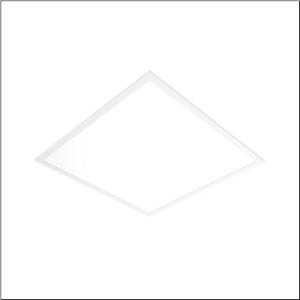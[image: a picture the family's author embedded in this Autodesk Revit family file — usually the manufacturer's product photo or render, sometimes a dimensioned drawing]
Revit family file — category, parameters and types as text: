
# Revit family: apollon_r__41_51mh11wm2443_3aa7
name_source: partatom
category: Lighting Fixtures
units: mm (PartAtom-declared; Revit-internal decimal feet)

## family parameters
Cut with Voids When Loaded = No
Host = Face
Light Source = No
Part Type = Normal
Room Calculation Point = No
Round Connector Dimension = Use Diameter
Shared = No

## types (1)
- --- (1 x LED, 4380 lm, 35 W, 4000K)
    Apparent Load = 35 VA
    CIE Flux Codes = 61 87 97 100 100
    Color Rendering = 80
    Color Temperature = 4000K
    Default Elevation = 1800 mm
    Description = Apollon® 41, office luminaire, primary optical cover: prismatic diffuser, of PS, light emission: direct distribution, primary light characteristic: symmetric, installation type: lay-in mounting, LED, rated luminous flux: 4.375lm, luminous efficacy: 125lm/W, light colour: 840, colour temperature: 4000K, control gear: ON/OFF Multilumen, with terminal, 3-pole, mains connection: 220..240V, AC, 50/60Hz, rated input power: 35W, suitable for self-contained emergency lighting element 58DB00B013A with integrated self-test function according to EN 60598-2-22, housing, of aluminium section, traffic white (RAL 9016), module: M625, length: 620mm, width: 620mm, height: 60mm, recess depth: 180mm, housing upper side, of sheet steel, protection rating (complete): IP20, protection rating (lamp compartment, on room side): IP40, insulation class (complete): insulation class II (safety insulation), certification: CE, ENEC, impact resistance: IK03, permissible operating ambient temperature: -25..+40°C, packaging unit: 1 piece
    Height = 0 mm  [stored 0 ft]
    Lamp = 1 x LED
    Lamp Light Flux = 4380 lm
    Lamp Power = 35 W
    Lamp count = 1
    Length = 620 mm
    Luminous efficacy = 125 lm/W
    Manufacturer = Siteco
    ModVariant = No
    Model = 51MH11WM2443
    Mounting Place = Ceiling
    Mounting Type = Recessed
    Number of Poles = 1
    OnlyDefault = Yes
    Power Factor = 1
    Product Name = Apollon® 41
    Product group = office luminaire | ceiling recessed
    ProductGroupID = 400
    Protection Class = Protection class II
    Protection Degree = IP 20
    RLX_Detail_Level = 1
    RLX_Emergency_Light_Flux = 0 lm
    RLX_Emergency_Type = 0
    RLX_Emergency_Type_DB = No
    RlxData = <blob elided: 13153 chars, md5=6666f8c4>
    Socket = socket
    Standby Power = 0 W
    System Light Flux = 4380 lm
    System Power = 35 W
    Type Comments = factory setting: luminous flux: 100 % | (ON | ON) | 900 mA
    Type Image = l_1291024.jpg
    URL = http://relux.com
    VarID = @adj_033123
    Voltage = 0 V
    Weight = 0.00 kg
    Width = 620 mm

note: [stored X ft] marks values corroborated as IEEE doubles in the binary element streams (Revit-internal decimal feet)

## geometry (parser evidence)
native form markers: Sweep x10
no freeform markers — native parametric forms only
